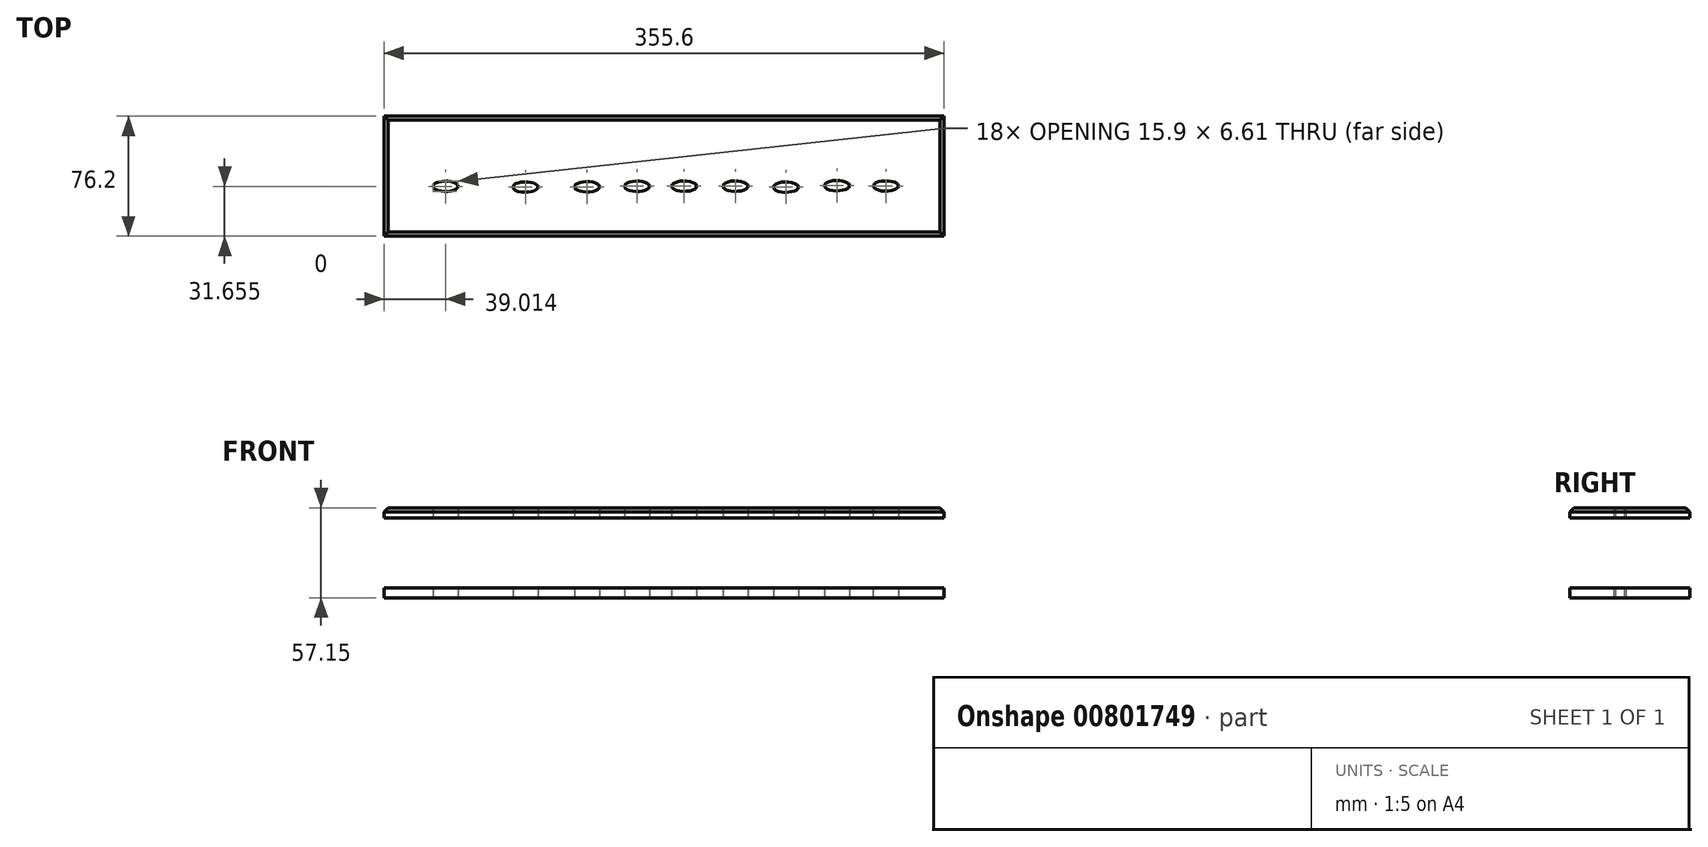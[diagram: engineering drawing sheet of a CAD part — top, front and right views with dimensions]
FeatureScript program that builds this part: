
annotation { "Feature Type Name" : "Feature", "Feature Type Description" : "" }
export const myFeature = defineFeature(function(context is Context, id is Id, definition is map)
    precondition{}
    {
        {
            var Q0;
            Q0=qCreatedBy(makeId("Top.planeOp"),FACE);
            var sketch = newSketch(context, id + "F0", { "sketchPlane" : qUnion([Q0])});
            skPoint(sketch, "E0", {"position": v(30.3, 12.95) * mm});
            skPoint(sketch, "E1", {"position": v(46.27, -0.98) * mm});
            skLineSegment(sketch, "E2.bottom", {"start": v(-160.28, 43.48) * mm, "end": v(195.32, 43.48) * mm});
            skLineSegment(sketch, "E2.top", {"start": v(-160.28, -32.72) * mm, "end": v(195.32, -32.72) * mm});
            skLineSegment(sketch, "E2.left", {"start": v(-160.28, 43.48) * mm, "end": v(-160.28, -32.72) * mm});
            skLineSegment(sketch, "E2.right", {"start": v(195.32, 43.48) * mm, "end": v(195.32, -32.72) * mm});
            skPoint(sketch, "E3", {"position": v(51.1, -0.98) * mm});
            skEllipse(sketch, "E4", {"center": v(-121.27, -1.06) * mm, "majorRadius": 7.95 * mm, "minorRadius": 3.3 * mm, "majorAxis": v(1, 0)});
            skEllipse(sketch, "E5", {"center": v(-70.51, -1.53) * mm, "majorRadius": 7.95 * mm, "minorRadius": 3.3 * mm, "majorAxis": v(1, 0)});
            skEllipse(sketch, "E6", {"center": v(-31.4, -1.37) * mm, "majorRadius": 7.95 * mm, "minorRadius": 3.3 * mm, "majorAxis": v(1, 0)});
            skEllipse(sketch, "E7", {"center": v(0.31, -1.02) * mm, "majorRadius": 7.95 * mm, "minorRadius": 3.3 * mm, "majorAxis": v(1, 0)});
            skEllipse(sketch, "E8", {"center": v(30.3, -0.98) * mm, "majorRadius": 7.95 * mm, "minorRadius": 3.3 * mm, "majorAxis": v(1, 0)});
            skEllipse(sketch, "E9", {"center": v(62.85, -0.98) * mm, "majorRadius": 7.95 * mm, "minorRadius": 3.3 * mm, "majorAxis": v(1, 0)});
            skEllipse(sketch, "E10", {"center": v(94.89, -1.59) * mm, "majorRadius": 7.95 * mm, "minorRadius": 3.3 * mm, "majorAxis": v(1, 0)});
            skEllipse(sketch, "E11", {"center": v(127.32, -0.61) * mm, "majorRadius": 7.95 * mm, "minorRadius": 3.3 * mm, "majorAxis": v(1, 0)});
            skEllipse(sketch, "E12", {"center": v(158.3, -0.85) * mm, "majorRadius": 7.95 * mm, "minorRadius": 3.3 * mm, "majorAxis": v(1, 0)});
            skLineSegment(sketch, "E13", {"start": v(-160.28, -1.49) * mm, "end": v(195.32, -1.49) * mm, "construction": true});
            skSolve(sketch);
        }
        {
            var Q0;
            Q0=makeQuery(id+"F0.imprint","IMPRINT",FACE,{"disambiguationData":[TD([[makeQuery(id+"F0.imprint","IMPRINT",EDGE,{"derivedFrom":sQuery(id+"F0.wireOp",EDGE,"E2.bottom")}),-1.0]])]});
            extrude(context, id + "F1", {"entities" : qUnion([Q0]), "depth" : 6.35 * mm, "offsetDistance" : 25.4 * mm});
        }
        {
            var Q0;
            Q0=makeQuery(id+"F1.opExtrude","SWEPT_BODY",BODY,{"disambiguationData":[OSD([sQuery(id+"F0.wireOp",EDGE,"E2.bottom"),sQuery(id+"F0.wireOp",EDGE,"E2.top"),sQuery(id+"F0.wireOp",EDGE,"E2.left"),sQuery(id+"F0.wireOp",EDGE,"E2.right"),sQuery(id+"F0.wireOp",EDGE,"E4"),sQuery(id+"F0.wireOp",EDGE,"E5"),sQuery(id+"F0.wireOp",EDGE,"E6"),sQuery(id+"F0.wireOp",EDGE,"E7"),sQuery(id+"F0.wireOp",EDGE,"E8"),sQuery(id+"F0.wireOp",EDGE,"E9"),sQuery(id+"F0.wireOp",EDGE,"E10"),sQuery(id+"F0.wireOp",EDGE,"E11"),sQuery(id+"F0.wireOp",EDGE,"E12")])]});
            transform(context, id + "F2", {"entities" : qUnion([Q0]), "transformType" : TransformType.TRANSLATION_3D, "dx" : 0 * mm, "dy" : 0 * mm, "dz" : -50.8 * mm, "makeCopy" : true});
        }
        {
            var Q0;
            Q0=makeQuery(id+"F1.opExtrude","CAP_EDGE",EDGE,{"disambiguationData":[OSD([sQuery(id+"F0.wireOp",EDGE,"E2.left")])],"isStart":false});
            var Q1;
            Q1=makeQuery(id+"F1.opExtrude","CAP_EDGE",EDGE,{"disambiguationData":[OSD([sQuery(id+"F0.wireOp",EDGE,"E2.top")])],"isStart":false});
            var Q2;
            Q2=makeQuery(id+"F1.opExtrude","CAP_EDGE",EDGE,{"disambiguationData":[OSD([sQuery(id+"F0.wireOp",EDGE,"E2.bottom")])],"isStart":false});
            var Q3;
            Q3=makeQuery(id+"F1.opExtrude","CAP_EDGE",EDGE,{"disambiguationData":[OSD([sQuery(id+"F0.wireOp",EDGE,"E2.right")])],"isStart":false});
            chamfer(context, id + "F3", {"entities" : qUnion([Q0, Q1, Q2, Q3]), "width" : 2.54 * mm, "tangentPropagation" : true});
        }
    });
